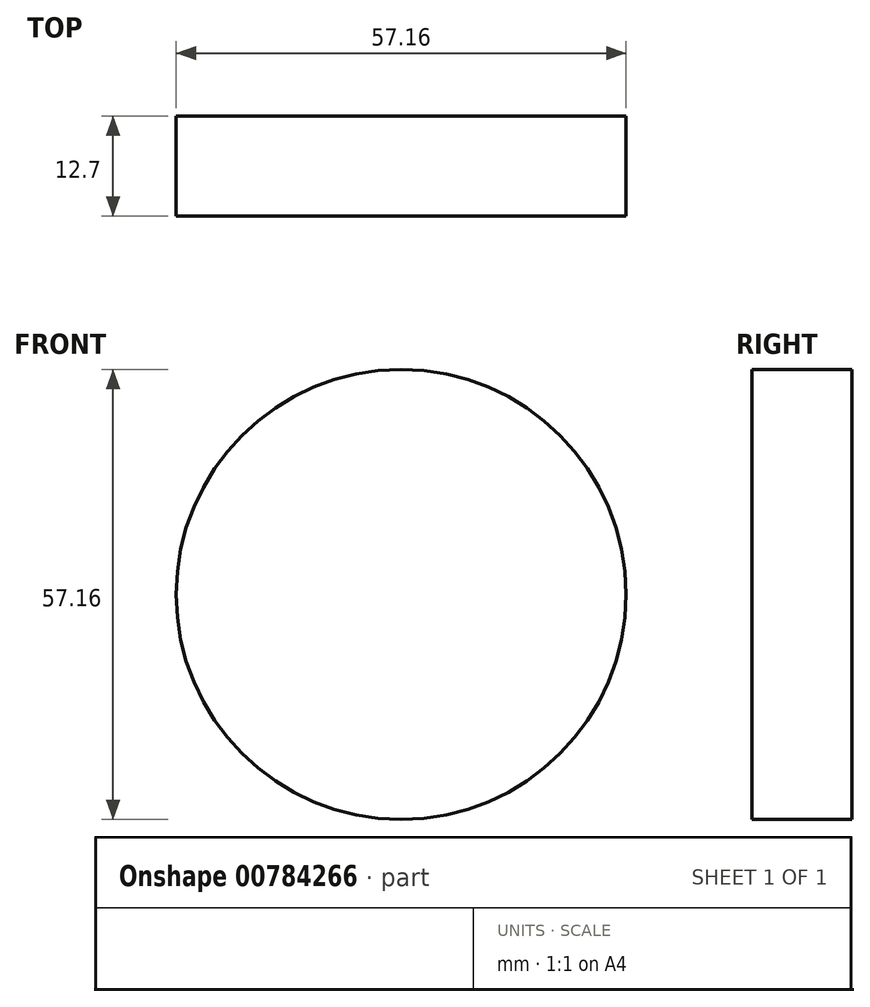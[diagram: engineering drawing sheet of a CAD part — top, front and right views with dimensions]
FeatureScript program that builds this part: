
annotation { "Feature Type Name" : "Feature", "Feature Type Description" : "" }
export const myFeature = defineFeature(function(context is Context, id is Id, definition is map)
    precondition{}
    {
        {
            var Q0;
            Q0=qCreatedBy(makeId("Front.planeOp"),FACE);
            var sketch = newSketch(context, id + "F0", { "sketchPlane" : qUnion([Q0])});
            skCircle(sketch, "E0", {"center": v(0, 0) * mm, "radius": 28.58 * mm});
            skSolve(sketch);
        }
        {
            var Q0;
            Q0 = qSketchRegion(id + "F0", true);
            extrude(context, id + "F1", {"entities" : qUnion([Q0]), "depth" : 12.7 * mm, "offsetDistance" : 25.4 * mm, "symmetric" : true});
        }
    });
